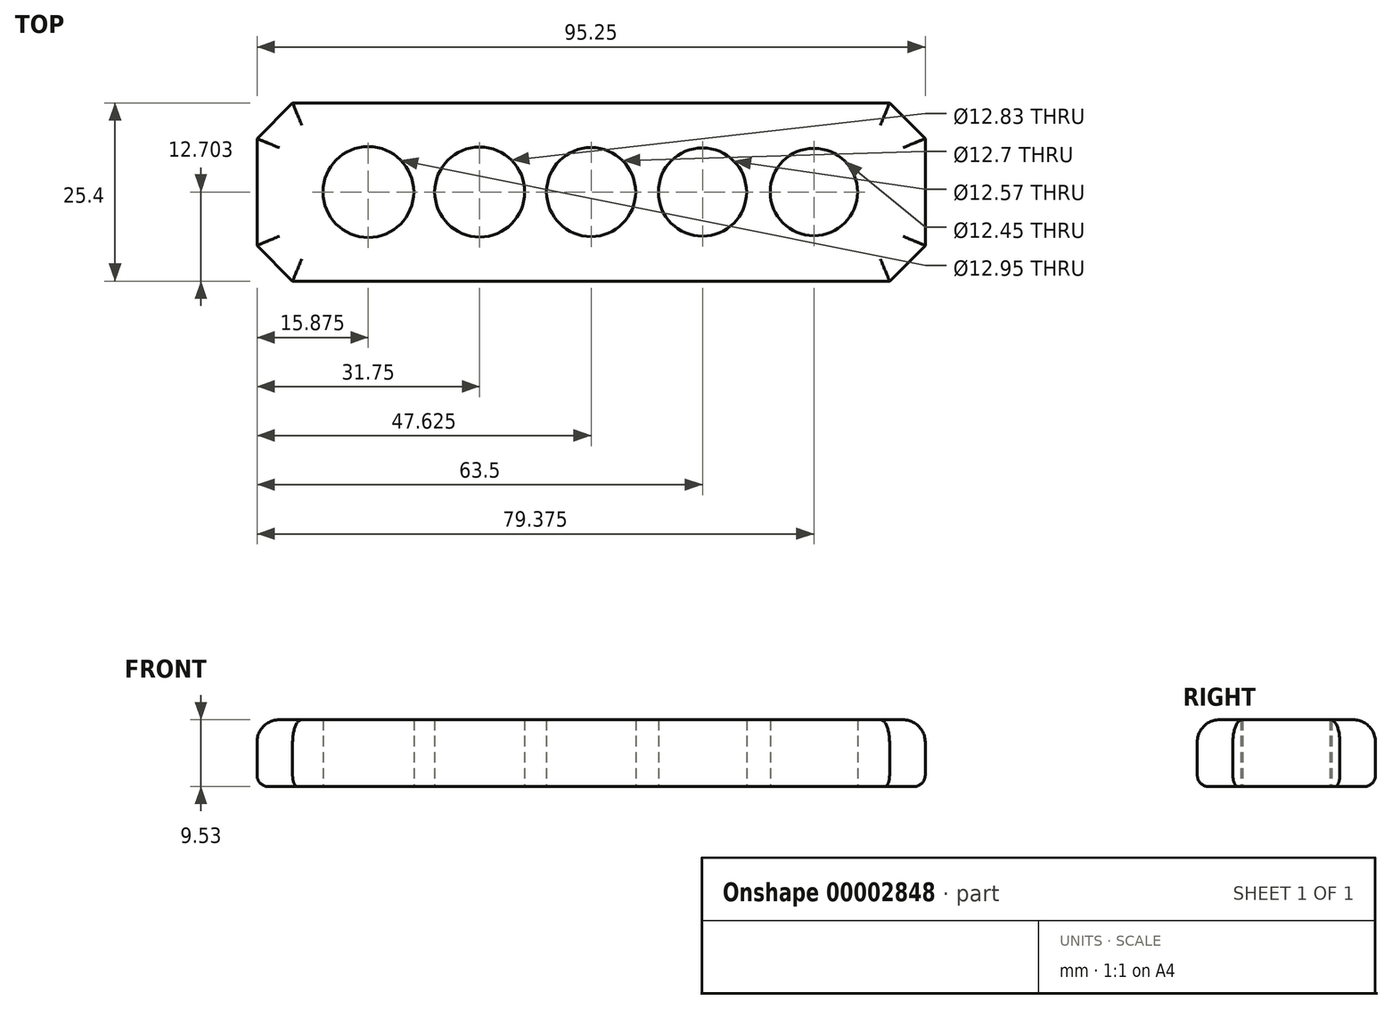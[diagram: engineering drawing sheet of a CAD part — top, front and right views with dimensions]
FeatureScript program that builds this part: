
annotation { "Feature Type Name" : "Feature", "Feature Type Description" : "" }
export const myFeature = defineFeature(function(context is Context, id is Id, definition is map)
    precondition{}
    {
        {
            var Q0;
            Q0=qCreatedBy(makeId("Top.planeOp"),FACE);
            var sketch = newSketch(context, id + "F0", { "sketchPlane" : qUnion([Q0])});
            skLineSegment(sketch, "E0.bottom", {"start": v(-57.15, 7.07) * mm, "end": v(38.1, 7.07) * mm});
            skLineSegment(sketch, "E0.top", {"start": v(-57.15, -18.33) * mm, "end": v(38.1, -18.33) * mm});
            skLineSegment(sketch, "E0.left", {"start": v(-57.15, 7.07) * mm, "end": v(-57.15, -18.33) * mm});
            skLineSegment(sketch, "E0.right", {"start": v(38.1, 7.07) * mm, "end": v(38.1, -18.33) * mm});
            skCircle(sketch, "E1", {"center": v(22.22, -5.63) * mm, "radius": 6.22 * mm});
            skCircle(sketch, "E2", {"center": v(6.35, -5.63) * mm, "radius": 6.29 * mm});
            skCircle(sketch, "E3", {"center": v(-9.53, -5.63) * mm, "radius": 6.35 * mm});
            skCircle(sketch, "E4", {"center": v(-25.4, -5.63) * mm, "radius": 6.41 * mm});
            skCircle(sketch, "E5", {"center": v(-41.28, -5.63) * mm, "radius": 6.48 * mm});
            skLineSegment(sketch, "E6", {"start": v(22.22, -5.63) * mm, "end": v(38.1, -5.63) * mm});
            skLineSegment(sketch, "E7", {"start": v(-41.28, -5.63) * mm, "end": v(-25.4, -5.63) * mm});
            skLineSegment(sketch, "E8", {"start": v(-25.4, -5.63) * mm, "end": v(-9.53, -5.63) * mm});
            skLineSegment(sketch, "E9", {"start": v(-9.53, -5.63) * mm, "end": v(6.35, -5.63) * mm});
            skLineSegment(sketch, "E10", {"start": v(6.35, -5.63) * mm, "end": v(22.22, -5.63) * mm});
            skSolve(sketch);
        }
        {
            var Q0;
            Q0=makeQuery(id+"F0.imprint","IMPRINT",FACE,{"disambiguationData":[TD([[makeQuery(id+"F0.imprint","IMPRINT",EDGE,{"derivedFrom":sQuery(id+"F0.wireOp",EDGE,"E0.bottom")}),-1.0]])]});
            extrude(context, id + "F1", {"entities" : qUnion([Q0]), "depth" : 9.52 * mm});
        }
        {
            var Q0;
            Q0=makeQuery(id+"F1.opExtrude","SWEPT_EDGE",EDGE,{"disambiguationData":[OSD([sQuery(id+"F0.wireOp",EDGE,"E0.top"),sQuery(id+"F0.wireOp",EDGE,"E0.left")])]});
            var Q1;
            Q1=makeQuery(id+"F1.opExtrude","SWEPT_EDGE",EDGE,{"disambiguationData":[OSD([sQuery(id+"F0.wireOp",EDGE,"E0.top"),sQuery(id+"F0.wireOp",EDGE,"E0.right")])]});
            var Q2;
            Q2=makeQuery(id+"F1.opExtrude","SWEPT_EDGE",EDGE,{"disambiguationData":[OSD([sQuery(id+"F0.wireOp",EDGE,"E0.bottom"),sQuery(id+"F0.wireOp",EDGE,"E0.right")])]});
            var Q3;
            Q3=makeQuery(id+"F1.opExtrude","SWEPT_EDGE",EDGE,{"disambiguationData":[OSD([sQuery(id+"F0.wireOp",EDGE,"E0.bottom"),sQuery(id+"F0.wireOp",EDGE,"E0.left")])]});
            chamfer(context, id + "F2", {"entities" : qUnion([Q0, Q1, Q2, Q3]), "width" : 5.08 * mm, "tangentPropagation" : true});
        }
        {
            var Q0;
            Q0=makeQuery(id+"F1.opExtrude","CAP_EDGE",EDGE,{"disambiguationData":[OSD([sQuery(id+"F0.wireOp",EDGE,"E0.bottom")])],"isStart":false});
            var Q1;
            {var subQ0=sQuery(id+"F0.wireOp",EDGE,"E0.bottom");var subQ1=sQuery(id+"F0.wireOp",EDGE,"E0.left");Q1=makeQuery(id+"F2.opChamfer","BLEND_EDGE",EDGE,{"blendedFrom":[makeQuery(id+"F1.opExtrude","SWEPT_EDGE",EDGE,{"disambiguationData":[OSD([subQ0,subQ1])]}),makeQuery(id+"F1.opExtrude","CAP_FACE",FACE,{"disambiguationData":[OSD([subQ0,sQuery(id+"F0.wireOp",EDGE,"E0.top"),subQ1,sQuery(id+"F0.wireOp",EDGE,"E0.right"),sQuery(id+"F0.wireOp",EDGE,"E1"),sQuery(id+"F0.wireOp",EDGE,"E2"),sQuery(id+"F0.wireOp",EDGE,"E3"),sQuery(id+"F0.wireOp",EDGE,"E4"),sQuery(id+"F0.wireOp",EDGE,"E5")])],"isStart":false})],"blendedInto":[makeQuery(id+"F1.opExtrude","CAP_FACE",FACE,{"disambiguationData":[OSD([subQ0,sQuery(id+"F0.wireOp",EDGE,"E0.top"),subQ1,sQuery(id+"F0.wireOp",EDGE,"E0.right"),sQuery(id+"F0.wireOp",EDGE,"E1"),sQuery(id+"F0.wireOp",EDGE,"E2"),sQuery(id+"F0.wireOp",EDGE,"E3"),sQuery(id+"F0.wireOp",EDGE,"E4"),sQuery(id+"F0.wireOp",EDGE,"E5")])],"isStart":false})]});}
            var Q2;
            Q2=makeQuery(id+"F1.opExtrude","CAP_EDGE",EDGE,{"disambiguationData":[OSD([sQuery(id+"F0.wireOp",EDGE,"E0.left")])],"isStart":false});
            var Q3;
            {var subQ0=sQuery(id+"F0.wireOp",EDGE,"E0.top");var subQ1=sQuery(id+"F0.wireOp",EDGE,"E0.left");Q3=makeQuery(id+"F2.opChamfer","BLEND_EDGE",EDGE,{"blendedFrom":[makeQuery(id+"F1.opExtrude","SWEPT_EDGE",EDGE,{"disambiguationData":[OSD([subQ0,subQ1])]}),makeQuery(id+"F1.opExtrude","CAP_FACE",FACE,{"disambiguationData":[OSD([sQuery(id+"F0.wireOp",EDGE,"E0.bottom"),subQ0,subQ1,sQuery(id+"F0.wireOp",EDGE,"E0.right"),sQuery(id+"F0.wireOp",EDGE,"E1"),sQuery(id+"F0.wireOp",EDGE,"E2"),sQuery(id+"F0.wireOp",EDGE,"E3"),sQuery(id+"F0.wireOp",EDGE,"E4"),sQuery(id+"F0.wireOp",EDGE,"E5")])],"isStart":false})],"blendedInto":[makeQuery(id+"F1.opExtrude","CAP_FACE",FACE,{"disambiguationData":[OSD([sQuery(id+"F0.wireOp",EDGE,"E0.bottom"),subQ0,subQ1,sQuery(id+"F0.wireOp",EDGE,"E0.right"),sQuery(id+"F0.wireOp",EDGE,"E1"),sQuery(id+"F0.wireOp",EDGE,"E2"),sQuery(id+"F0.wireOp",EDGE,"E3"),sQuery(id+"F0.wireOp",EDGE,"E4"),sQuery(id+"F0.wireOp",EDGE,"E5")])],"isStart":false})]});}
            var Q4;
            Q4=makeQuery(id+"F1.opExtrude","CAP_EDGE",EDGE,{"disambiguationData":[OSD([sQuery(id+"F0.wireOp",EDGE,"E0.top")])],"isStart":false});
            var Q5;
            {var subQ0=sQuery(id+"F0.wireOp",EDGE,"E0.top");var subQ1=sQuery(id+"F0.wireOp",EDGE,"E0.right");Q5=makeQuery(id+"F2.opChamfer","BLEND_EDGE",EDGE,{"blendedFrom":[makeQuery(id+"F1.opExtrude","SWEPT_EDGE",EDGE,{"disambiguationData":[OSD([subQ0,subQ1])]}),makeQuery(id+"F1.opExtrude","CAP_FACE",FACE,{"disambiguationData":[OSD([sQuery(id+"F0.wireOp",EDGE,"E0.bottom"),subQ0,sQuery(id+"F0.wireOp",EDGE,"E0.left"),subQ1,sQuery(id+"F0.wireOp",EDGE,"E1"),sQuery(id+"F0.wireOp",EDGE,"E2"),sQuery(id+"F0.wireOp",EDGE,"E3"),sQuery(id+"F0.wireOp",EDGE,"E4"),sQuery(id+"F0.wireOp",EDGE,"E5")])],"isStart":false})],"blendedInto":[makeQuery(id+"F1.opExtrude","CAP_FACE",FACE,{"disambiguationData":[OSD([sQuery(id+"F0.wireOp",EDGE,"E0.bottom"),subQ0,sQuery(id+"F0.wireOp",EDGE,"E0.left"),subQ1,sQuery(id+"F0.wireOp",EDGE,"E1"),sQuery(id+"F0.wireOp",EDGE,"E2"),sQuery(id+"F0.wireOp",EDGE,"E3"),sQuery(id+"F0.wireOp",EDGE,"E4"),sQuery(id+"F0.wireOp",EDGE,"E5")])],"isStart":false})]});}
            var Q6;
            Q6=makeQuery(id+"F1.opExtrude","CAP_EDGE",EDGE,{"disambiguationData":[OSD([sQuery(id+"F0.wireOp",EDGE,"E0.right")])],"isStart":false});
            var Q7;
            {var subQ0=sQuery(id+"F0.wireOp",EDGE,"E0.bottom");var subQ1=sQuery(id+"F0.wireOp",EDGE,"E0.right");Q7=makeQuery(id+"F2.opChamfer","BLEND_EDGE",EDGE,{"blendedFrom":[makeQuery(id+"F1.opExtrude","SWEPT_EDGE",EDGE,{"disambiguationData":[OSD([subQ0,subQ1])]}),makeQuery(id+"F1.opExtrude","CAP_FACE",FACE,{"disambiguationData":[OSD([subQ0,sQuery(id+"F0.wireOp",EDGE,"E0.top"),sQuery(id+"F0.wireOp",EDGE,"E0.left"),subQ1,sQuery(id+"F0.wireOp",EDGE,"E1"),sQuery(id+"F0.wireOp",EDGE,"E2"),sQuery(id+"F0.wireOp",EDGE,"E3"),sQuery(id+"F0.wireOp",EDGE,"E4"),sQuery(id+"F0.wireOp",EDGE,"E5")])],"isStart":false})],"blendedInto":[makeQuery(id+"F1.opExtrude","CAP_FACE",FACE,{"disambiguationData":[OSD([subQ0,sQuery(id+"F0.wireOp",EDGE,"E0.top"),sQuery(id+"F0.wireOp",EDGE,"E0.left"),subQ1,sQuery(id+"F0.wireOp",EDGE,"E1"),sQuery(id+"F0.wireOp",EDGE,"E2"),sQuery(id+"F0.wireOp",EDGE,"E3"),sQuery(id+"F0.wireOp",EDGE,"E4"),sQuery(id+"F0.wireOp",EDGE,"E5")])],"isStart":false})]});}
            fillet(context, id + "F3", {"entities" : qUnion([Q0, Q1, Q2, Q3, Q4, Q5, Q6, Q7]), "radius" : 3.17 * mm, "tangentPropagation" : true, "allowEdgeOverflow" : false});
        }
        {
            var Q0;
            Q0=makeQuery(id+"F1.opExtrude","CAP_EDGE",EDGE,{"disambiguationData":[OSD([sQuery(id+"F0.wireOp",EDGE,"E0.top")])],"isStart":true});
            var Q1;
            {var subQ0=sQuery(id+"F0.wireOp",EDGE,"E0.top");var subQ1=sQuery(id+"F0.wireOp",EDGE,"E0.left");Q1=makeQuery(id+"F2.opChamfer","BLEND_EDGE",EDGE,{"blendedFrom":[makeQuery(id+"F1.opExtrude","SWEPT_EDGE",EDGE,{"disambiguationData":[OSD([subQ0,subQ1])]}),makeQuery(id+"F1.opExtrude","CAP_FACE",FACE,{"disambiguationData":[OSD([sQuery(id+"F0.wireOp",EDGE,"E0.bottom"),subQ0,subQ1,sQuery(id+"F0.wireOp",EDGE,"E0.right"),sQuery(id+"F0.wireOp",EDGE,"E1"),sQuery(id+"F0.wireOp",EDGE,"E2"),sQuery(id+"F0.wireOp",EDGE,"E3"),sQuery(id+"F0.wireOp",EDGE,"E4"),sQuery(id+"F0.wireOp",EDGE,"E5")])],"isStart":true})],"blendedInto":[makeQuery(id+"F1.opExtrude","CAP_FACE",FACE,{"disambiguationData":[OSD([sQuery(id+"F0.wireOp",EDGE,"E0.bottom"),subQ0,subQ1,sQuery(id+"F0.wireOp",EDGE,"E0.right"),sQuery(id+"F0.wireOp",EDGE,"E1"),sQuery(id+"F0.wireOp",EDGE,"E2"),sQuery(id+"F0.wireOp",EDGE,"E3"),sQuery(id+"F0.wireOp",EDGE,"E4"),sQuery(id+"F0.wireOp",EDGE,"E5")])],"isStart":true})]});}
            var Q2;
            Q2=makeQuery(id+"F1.opExtrude","CAP_EDGE",EDGE,{"disambiguationData":[OSD([sQuery(id+"F0.wireOp",EDGE,"E0.left")])],"isStart":true});
            var Q3;
            {var subQ0=sQuery(id+"F0.wireOp",EDGE,"E0.bottom");var subQ1=sQuery(id+"F0.wireOp",EDGE,"E0.left");Q3=makeQuery(id+"F2.opChamfer","BLEND_EDGE",EDGE,{"blendedFrom":[makeQuery(id+"F1.opExtrude","SWEPT_EDGE",EDGE,{"disambiguationData":[OSD([subQ0,subQ1])]}),makeQuery(id+"F1.opExtrude","CAP_FACE",FACE,{"disambiguationData":[OSD([subQ0,sQuery(id+"F0.wireOp",EDGE,"E0.top"),subQ1,sQuery(id+"F0.wireOp",EDGE,"E0.right"),sQuery(id+"F0.wireOp",EDGE,"E1"),sQuery(id+"F0.wireOp",EDGE,"E2"),sQuery(id+"F0.wireOp",EDGE,"E3"),sQuery(id+"F0.wireOp",EDGE,"E4"),sQuery(id+"F0.wireOp",EDGE,"E5")])],"isStart":true})],"blendedInto":[makeQuery(id+"F1.opExtrude","CAP_FACE",FACE,{"disambiguationData":[OSD([subQ0,sQuery(id+"F0.wireOp",EDGE,"E0.top"),subQ1,sQuery(id+"F0.wireOp",EDGE,"E0.right"),sQuery(id+"F0.wireOp",EDGE,"E1"),sQuery(id+"F0.wireOp",EDGE,"E2"),sQuery(id+"F0.wireOp",EDGE,"E3"),sQuery(id+"F0.wireOp",EDGE,"E4"),sQuery(id+"F0.wireOp",EDGE,"E5")])],"isStart":true})]});}
            var Q4;
            Q4=makeQuery(id+"F1.opExtrude","CAP_EDGE",EDGE,{"disambiguationData":[OSD([sQuery(id+"F0.wireOp",EDGE,"E0.bottom")])],"isStart":true});
            var Q5;
            {var subQ0=sQuery(id+"F0.wireOp",EDGE,"E0.bottom");var subQ1=sQuery(id+"F0.wireOp",EDGE,"E0.right");Q5=makeQuery(id+"F2.opChamfer","BLEND_EDGE",EDGE,{"blendedFrom":[makeQuery(id+"F1.opExtrude","SWEPT_EDGE",EDGE,{"disambiguationData":[OSD([subQ0,subQ1])]}),makeQuery(id+"F1.opExtrude","CAP_FACE",FACE,{"disambiguationData":[OSD([subQ0,sQuery(id+"F0.wireOp",EDGE,"E0.top"),sQuery(id+"F0.wireOp",EDGE,"E0.left"),subQ1,sQuery(id+"F0.wireOp",EDGE,"E1"),sQuery(id+"F0.wireOp",EDGE,"E2"),sQuery(id+"F0.wireOp",EDGE,"E3"),sQuery(id+"F0.wireOp",EDGE,"E4"),sQuery(id+"F0.wireOp",EDGE,"E5")])],"isStart":true})],"blendedInto":[makeQuery(id+"F1.opExtrude","CAP_FACE",FACE,{"disambiguationData":[OSD([subQ0,sQuery(id+"F0.wireOp",EDGE,"E0.top"),sQuery(id+"F0.wireOp",EDGE,"E0.left"),subQ1,sQuery(id+"F0.wireOp",EDGE,"E1"),sQuery(id+"F0.wireOp",EDGE,"E2"),sQuery(id+"F0.wireOp",EDGE,"E3"),sQuery(id+"F0.wireOp",EDGE,"E4"),sQuery(id+"F0.wireOp",EDGE,"E5")])],"isStart":true})]});}
            var Q6;
            Q6=makeQuery(id+"F1.opExtrude","CAP_EDGE",EDGE,{"disambiguationData":[OSD([sQuery(id+"F0.wireOp",EDGE,"E0.right")])],"isStart":true});
            var Q7;
            {var subQ0=sQuery(id+"F0.wireOp",EDGE,"E0.top");var subQ1=sQuery(id+"F0.wireOp",EDGE,"E0.right");Q7=makeQuery(id+"F2.opChamfer","BLEND_EDGE",EDGE,{"blendedFrom":[makeQuery(id+"F1.opExtrude","SWEPT_EDGE",EDGE,{"disambiguationData":[OSD([subQ0,subQ1])]}),makeQuery(id+"F1.opExtrude","CAP_FACE",FACE,{"disambiguationData":[OSD([sQuery(id+"F0.wireOp",EDGE,"E0.bottom"),subQ0,sQuery(id+"F0.wireOp",EDGE,"E0.left"),subQ1,sQuery(id+"F0.wireOp",EDGE,"E1"),sQuery(id+"F0.wireOp",EDGE,"E2"),sQuery(id+"F0.wireOp",EDGE,"E3"),sQuery(id+"F0.wireOp",EDGE,"E4"),sQuery(id+"F0.wireOp",EDGE,"E5")])],"isStart":true})],"blendedInto":[makeQuery(id+"F1.opExtrude","CAP_FACE",FACE,{"disambiguationData":[OSD([sQuery(id+"F0.wireOp",EDGE,"E0.bottom"),subQ0,sQuery(id+"F0.wireOp",EDGE,"E0.left"),subQ1,sQuery(id+"F0.wireOp",EDGE,"E1"),sQuery(id+"F0.wireOp",EDGE,"E2"),sQuery(id+"F0.wireOp",EDGE,"E3"),sQuery(id+"F0.wireOp",EDGE,"E4"),sQuery(id+"F0.wireOp",EDGE,"E5")])],"isStart":true})]});}
            fillet(context, id + "F4", {"entities" : qUnion([Q0, Q1, Q2, Q3, Q4, Q5, Q6, Q7]), "radius" : 1.59 * mm, "tangentPropagation" : true, "allowEdgeOverflow" : false});
        }
    });
